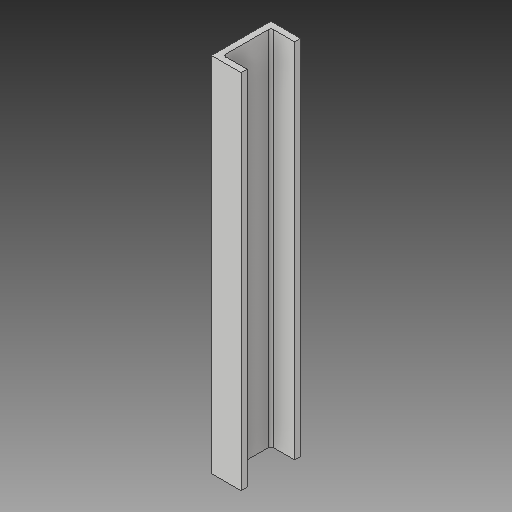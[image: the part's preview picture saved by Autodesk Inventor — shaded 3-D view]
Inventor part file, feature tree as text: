
AUTODESK INVENTOR PART (.ipt)
format: ipt  version: 2019 (Build 230136000, 136)  size: 117,760 bytes
history: native  units: mm
features: extrude x2, sketch x2, fillet x1
ambient origin geometry x8: Origin, YZ Plane, XZ Plane, XY Plane, X Axis, Y Axis, Z Axis, Center Point
bodies: Solid1 (feature_tree)
feature tree (5):
  extrude  "Extrusion1"  Depth=100.0mm
  extrude  "Extrusion2"  Depth=80.0mm
  fillet  "Fillet1"  Radius=40.0mm
  sketch  "Sketch1"  dims[d0=610.0mm d1=100.0mm]
  sketch  "Sketch2"  dims[d2=50.0mm d3=0.0mm d4=80.0mm d5=40.0mm d6=0.0mm d7=4.0mm]
